# Revit family: NBS_CordekLtd_Arbrcks_AirBrickandAdjustableCavityVent
name_source: partatom
category: Specialty Equipment
revit_build: Autodesk Revit 2014 (Build: 20131024_2115(x64)
units: mm (PartAtom-declared; Revit-internal decimal feet)

## types (1)
- AirBrickAndAdjustableCavityVent
    Accessories = CGV-012 - Adjustable sleeve horizontal, CGV-013 - Adjustable sleeve vertical
    AdjustableCavityVentMaterial = NBS_Concept
    AirBrickColourOptions = Blue/Black, Buff, Terracotta
    AirBrickFreeAirFlow = 7600 mm²
    AirBrickMaterial = NBS_Concept
    AirBrickSize = 210 x 70 x 57 mm (l x h x d):
    Apertures = Louvre
    AssetType = Fixed
    BIMObjectName = NBS_CordekLtd_Airbricks_AirBrickandAdjustableCavityVent
    Category = Pr_35_90_50_03:Airbricks
    Color = Adjustable Cavity Vent: Black
    Depth = 250.5 mm  [stored 0.82185 ft]
    Description = Polypropylene air brick and adjustable cavity vent
    DurationUnit = year
    Features = Incorporates a front mounted grill, comprising evenly spaced voids, designed to resist blockage by debris
    IfcExportAs = IfcBuildingElementProxyType
    IfcExportType = USERDEFINED
    ManufacturerName = Cordek Ltd
    ManufacturerURL = www.cordek.com
    Material = Injection moulded polypropylene
    ModelReference = Air Brick and Adjustable Cavity Vent
    NBSCertification = http://www.nationalbimlibrary.com
    NBSDescription = Airbricks
    NBSReference = 45-80-50/370
    Name = Airbricks_AirBrickandAdjustableCavityVent_CordekLtd
    NominalHeight = 250.5 mm  [stored 0.82185 ft]
    NominalWidth = 230 mm
    ProductInformation = www.cordek.com/uploads/data_sheets/M-DS18_air_brick_and_cavity_vent_data_sheet_v2_cordek.pdf
    Uniclass2 = 45-91-50/403
    Uniclass2015Description = Airbricks
    Uniclass2015Reference = Pr_35_90_50_03
    Uniclass2015Version = Products v1.1
    Version = 1
    WarrantyDurationUnit = year
    Width = 230 mm

note: [stored X ft] marks values corroborated as IEEE doubles in the binary element streams (Revit-internal decimal feet)

## geometry (parser evidence)
native form markers: Sweep x1
no freeform markers — native parametric forms only
